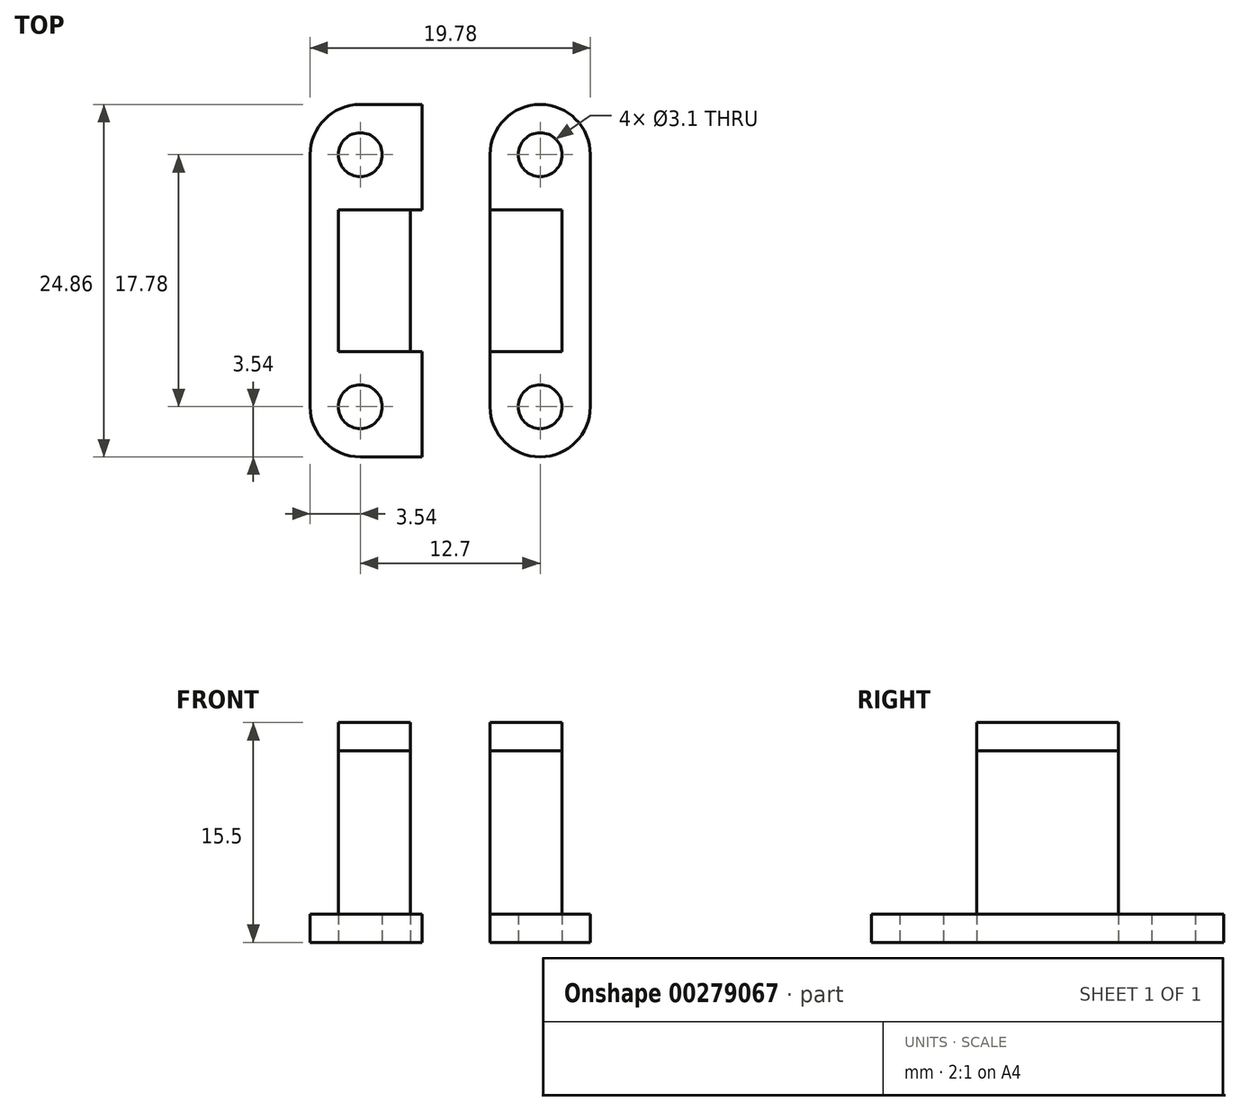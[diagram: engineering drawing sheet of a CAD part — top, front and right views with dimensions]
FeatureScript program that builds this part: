
annotation { "Feature Type Name" : "Feature", "Feature Type Description" : "" }
export const myFeature = defineFeature(function(context is Context, id is Id, definition is map)
    precondition{}
    {
        {
            var Q0;
            Q0=qCreatedBy(makeId("Top.planeOp"),FACE);
            var sketch = newSketch(context, id + "F0", { "sketchPlane" : qUnion([Q0])});
            skLineSegment(sketch, "E0.bottom", {"start": v(0, -12.43) * mm, "end": v(0, -12.43) * mm});
            skLineSegment(sketch, "E0.top", {"start": v(0, 12.43) * mm, "end": v(0, 12.43) * mm});
            skLineSegment(sketch, "E0.left", {"start": v(3.54, -8.9) * mm, "end": v(3.54, 8.9) * mm});
            skLineSegment(sketch, "E0.right", {"start": v(-3.54, -8.89) * mm, "end": v(-3.54, 8.89) * mm});
            skPoint(sketch, "E0.middle", {"position": v(0, 0) * mm});
            skLineSegment(sketch, "E1", {"start": v(-7.16, -8.9) * mm, "end": v(6.8, -8.9) * mm, "construction": true});
            skLineSegment(sketch, "E2", {"start": v(-9.41, 8.9) * mm, "end": v(8.22, 8.9) * mm, "construction": true});
            skCircle(sketch, "E3", {"center": v(0, 8.9) * mm, "radius": 1.55 * mm});
            skCircle(sketch, "E4", {"center": v(0, -8.9) * mm, "radius": 1.55 * mm});
            skPoint(sketch, "E4.centerSnap0", {"position": v(0, -12.43) * mm});
            skPoint(sketch, "E5.visualSharp", {"position": v(3.54, -12.43) * mm});
            skArc(sketch, "E5.filletArc", {"start": v(0, -12.43) * mm, "mid": v(2.5, -11.4) * mm, "end": v(3.54, -8.9) * mm});
            skPoint(sketch, "E6.visualSharp", {"position": v(-3.54, -12.43) * mm});
            skArc(sketch, "E6.filletArc", {"start": v(-3.25, -10.3) * mm, "mid": v(-1.94, -11.85) * mm, "end": v(0, -12.43) * mm});
            skPoint(sketch, "E7.visualSharp", {"position": v(-3.54, -8.9) * mm});
            skArc(sketch, "E7.filletArc", {"start": v(-3.54, -8.89) * mm, "mid": v(-3.47, -9.6) * mm, "end": v(-3.25, -10.3) * mm});
            skPoint(sketch, "E8.visualSharp", {"position": v(-3.54, 12.43) * mm});
            skArc(sketch, "E8.filletArc", {"start": v(0, 12.43) * mm, "mid": v(-2.5, 11.4) * mm, "end": v(-3.54, 8.89) * mm});
            skPoint(sketch, "E9.visualSharp", {"position": v(3.54, 12.43) * mm});
            skArc(sketch, "E9.filletArc", {"start": v(3.54, 8.9) * mm, "mid": v(2.5, 11.4) * mm, "end": v(0, 12.43) * mm});
            skLineSegment(sketch, "E10", {"start": v(6.35, 22.18) * mm, "end": v(6.35, -17.31) * mm, "construction": true});
            skArc(sketch, "E11.MirrorCS", {"start": v(16.24, -8.89) * mm, "mid": v(16.17, -9.6) * mm, "end": v(15.95, -10.3) * mm});
            skPoint(sketch, "E12.MirrorP", {"position": v(12.7, -12.43) * mm});
            skLineSegment(sketch, "E13.MirrorCS", {"start": v(16.24, -8.89) * mm, "end": v(16.24, 8.9) * mm});
            skLineSegment(sketch, "E14.MirrorCS", {"start": v(9.16, -8.89) * mm, "end": v(9.16, 8.9) * mm});
            skPoint(sketch, "E15.MirrorP", {"position": v(12.7, 0) * mm});
            skCircle(sketch, "E16.MirrorC", {"center": v(12.7, 8.9) * mm, "radius": 1.55 * mm});
            skCircle(sketch, "E17.MirrorC", {"center": v(12.7, -8.89) * mm, "radius": 1.55 * mm});
            skArc(sketch, "E18.MirrorCS", {"start": v(12.7, -12.43) * mm, "mid": v(10.2, -11.4) * mm, "end": v(9.16, -8.89) * mm});
            skArc(sketch, "E19.MirrorCS", {"start": v(15.95, -10.3) * mm, "mid": v(14.64, -11.85) * mm, "end": v(12.7, -12.43) * mm});
            skArc(sketch, "E20.MirrorCS", {"start": v(12.7, 12.43) * mm, "mid": v(15.2, 11.4) * mm, "end": v(16.24, 8.9) * mm});
            skArc(sketch, "E21.MirrorCS", {"start": v(9.16, 8.9) * mm, "mid": v(10.2, 11.4) * mm, "end": v(12.7, 12.43) * mm});
            skPoint(sketch, "E22.MirrorP", {"position": v(16.24, -12.43) * mm});
            skPoint(sketch, "E23.MirrorP", {"position": v(9.16, -12.43) * mm});
            skPoint(sketch, "E24.MirrorP", {"position": v(16.24, 12.43) * mm});
            skPoint(sketch, "E25.MirrorP", {"position": v(9.16, 12.43) * mm});
            skPoint(sketch, "E26.MirrorP", {"position": v(16.24, -8.89) * mm});
            skLineSegment(sketch, "E27", {"start": v(0, 12.43) * mm, "end": v(4.35, 12.43) * mm});
            skLineSegment(sketch, "E28", {"start": v(0, -12.43) * mm, "end": v(4.35, -12.43) * mm});
            skLineSegment(sketch, "E29", {"start": v(4.35, -12.43) * mm, "end": v(4.35, 12.43) * mm});
            skLineSegment(sketch, "E30", {"start": v(12.7, -12.43) * mm, "end": v(8.35, -12.43) * mm});
            skLineSegment(sketch, "E31", {"start": v(12.7, 12.43) * mm, "end": v(8.35, 12.43) * mm});
            skLineSegment(sketch, "E32", {"start": v(8.35, 12.43) * mm, "end": v(8.35, -12.43) * mm});
            skLineSegment(sketch, "E33", {"start": v(-1.54, 5) * mm, "end": v(4.35, 5) * mm});
            skLineSegment(sketch, "E34", {"start": v(-1.54, -5) * mm, "end": v(4.35, -5) * mm});
            skLineSegment(sketch, "E35", {"start": v(-1.54, 5) * mm, "end": v(-1.54, -5) * mm});
            skLineSegment(sketch, "E36", {"start": v(4.35, 5) * mm, "end": v(4.35, -5) * mm});
            skLineSegment(sketch, "E37.MirrorCS", {"start": v(8.35, 5) * mm, "end": v(8.35, -5) * mm});
            skLineSegment(sketch, "E38.MirrorCS", {"start": v(14.24, -5) * mm, "end": v(8.35, -5) * mm});
            skLineSegment(sketch, "E39.MirrorCS", {"start": v(14.24, 5) * mm, "end": v(8.35, 5) * mm});
            skLineSegment(sketch, "E40.MirrorCS", {"start": v(14.24, 5) * mm, "end": v(14.24, -5) * mm});
            skLineSegment(sketch, "E41", {"start": v(4.35, -5) * mm, "end": v(8.35, -5) * mm});
            skLineSegment(sketch, "E42", {"start": v(4.35, 5) * mm, "end": v(8.35, 5) * mm});
            skSolve(sketch);
        }
        {
            var Q0;
            Q0=makeQuery(id+"F0.imprint","IMPRINT",FACE,{"disambiguationData":[TD([[makeQuery(id+"F0.imprint","IMPRINT",EDGE,{"derivedFrom":sQuery(id+"F0.wireOp",EDGE,"E0.left")}),1.0]])]});
            var Q1;
            {var subQ1=sQuery(id+"F0.wireOp",EDGE,"E9.filletArc");Q1=makeQuery(id+"F0.imprint","IMPRINT",FACE,{"disambiguationData":[TD([[makeQuery(id+"F0.imprint","IMPRINT",EDGE,{"derivedFrom":subQ1}),-1.0]])]});}
            var Q2;
            {var subQ4=sQuery(id+"F0.wireOp",EDGE,"E5.filletArc");Q2=makeQuery(id+"F0.imprint","IMPRINT",FACE,{"disambiguationData":[TD([[makeQuery(id+"F0.imprint","IMPRINT",EDGE,{"derivedFrom":subQ4}),-1.0]])]});}
            var Q3;
            {var subQ1=sQuery(id+"F0.wireOp",EDGE,"E18.MirrorCS");Q3=makeQuery(id+"F0.imprint","IMPRINT",FACE,{"disambiguationData":[TD([[makeQuery(id+"F0.imprint","IMPRINT",EDGE,{"derivedFrom":subQ1}),1.0]])]});}
            var Q4;
            Q4=makeQuery(id+"F0.imprint","IMPRINT",FACE,{"disambiguationData":[TD([[makeQuery(id+"F0.imprint","IMPRINT",EDGE,{"derivedFrom":sQuery(id+"F0.wireOp",EDGE,"E11.MirrorCS")}),-1.0]])]});
            var Q5;
            {var subQ0=sQuery(id+"F0.wireOp",EDGE,"E21.MirrorCS");Q5=makeQuery(id+"F0.imprint","IMPRINT",FACE,{"disambiguationData":[TD([[makeQuery(id+"F0.imprint","IMPRINT",EDGE,{"derivedFrom":subQ0}),1.0]])]});}
            extrude(context, id + "F1", {"entities" : qUnion([Q0, Q1, Q2, Q3, Q4, Q5]), "depth" : 2 * mm});
        }
        {
            var Q0;
            {var subQ5=sQuery(id+"F0.wireOp",EDGE,"E35");Q0=makeQuery(id+"F0.imprint","IMPRINT",FACE,{"disambiguationData":[TD([[makeQuery(id+"F0.imprint","IMPRINT",EDGE,{"derivedFrom":subQ5}),1.0]])]});}
            var Q1;
            {var subQ5=sQuery(id+"F0.wireOp",EDGE,"E40.MirrorCS");Q1=makeQuery(id+"F0.imprint","IMPRINT",FACE,{"disambiguationData":[TD([[makeQuery(id+"F0.imprint","IMPRINT",EDGE,{"derivedFrom":subQ5}),-1.0]])]});}
            var Q2;
            {var subQ5=sQuery(id+"F0.wireOp",EDGE,"E36");Q2=makeQuery(id+"F0.imprint","IMPRINT",FACE,{"disambiguationData":[TD([[makeQuery(id+"F0.imprint","IMPRINT",EDGE,{"derivedFrom":subQ5}),-1.0]])]});}
            var Q3;
            {var subQ5=sQuery(id+"F0.wireOp",EDGE,"E37.MirrorCS");Q3=makeQuery(id+"F0.imprint","IMPRINT",FACE,{"disambiguationData":[TD([[makeQuery(id+"F0.imprint","IMPRINT",EDGE,{"derivedFrom":subQ5}),1.0]])]});}
            extrude(context, id + "F2", {"entities" : qUnion([Q0, Q1, Q2, Q3]), "depth" : 13.5 * mm});
        }
        {
            var Q0;
            {var subQ5=sQuery(id+"F0.wireOp",EDGE,"E40.MirrorCS");Q0=makeQuery(id+"F0.imprint","IMPRINT",FACE,{"disambiguationData":[TD([[makeQuery(id+"F0.imprint","IMPRINT",EDGE,{"derivedFrom":subQ5}),-1.0]])]});}
            var Q1;
            Q1=makeQuery(id+"F0.imprint","IMPRINT",FACE,{"disambiguationData":[TD([[makeQuery(id+"F0.imprint","IMPRINT",EDGE,{"derivedFrom":sQuery(id+"F0.wireOp",EDGE,"E36")}),1.0]])]});
            var Q2;
            {var subQ5=sQuery(id+"F0.wireOp",EDGE,"E35");Q2=makeQuery(id+"F0.imprint","IMPRINT",FACE,{"disambiguationData":[TD([[makeQuery(id+"F0.imprint","IMPRINT",EDGE,{"derivedFrom":subQ5}),1.0]])]});}
            var Q3;
            {var subQ5=sQuery(id+"F0.wireOp",EDGE,"E36");Q3=makeQuery(id+"F0.imprint","IMPRINT",FACE,{"disambiguationData":[TD([[makeQuery(id+"F0.imprint","IMPRINT",EDGE,{"derivedFrom":subQ5}),-1.0]])]});}
            var Q4;
            {var subQ5=sQuery(id+"F0.wireOp",EDGE,"E37.MirrorCS");Q4=makeQuery(id+"F0.imprint","IMPRINT",FACE,{"disambiguationData":[TD([[makeQuery(id+"F0.imprint","IMPRINT",EDGE,{"derivedFrom":subQ5}),1.0]])]});}
            extrude(context, id + "F3", {"entities" : qUnion([Q0, Q1, Q2, Q3, Q4]), "depth" : 15.5 * mm, "hasSecondDirection" : true, "secondDirectionOppositeDirection" : false, "secondDirectionDepth" : 13.5 * mm});
        }
    });
